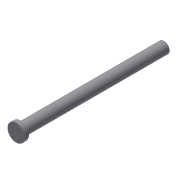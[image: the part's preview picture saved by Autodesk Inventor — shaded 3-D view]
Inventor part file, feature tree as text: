
AUTODESK INVENTOR PART (.ipt)
format: ipt  version: 2014 (Build 180170000, 170)  size: 72,704 bytes
history: native  units: mm
features: revolve x1, sketch x1
ambient origin geometry x8: Origin, YZ Plane, XZ Plane, XY Plane, X Axis, Y Axis, Z Axis, Center Point
bodies: Solid1 (feature_tree)
feature tree (2):
  revolve  "Revolution1"  [1 undecoded]
  sketch  "Sketch1"  dims[d0=2.0mm d1=3.0mm d2=1.5mm d3=50.0mm d4=90.0deg]
note: 1 required parameter value undecoded (feature->parameter linkage not recoverable at this tier; creation-order binding heuristic only, values carry confidence <= 0.55)
